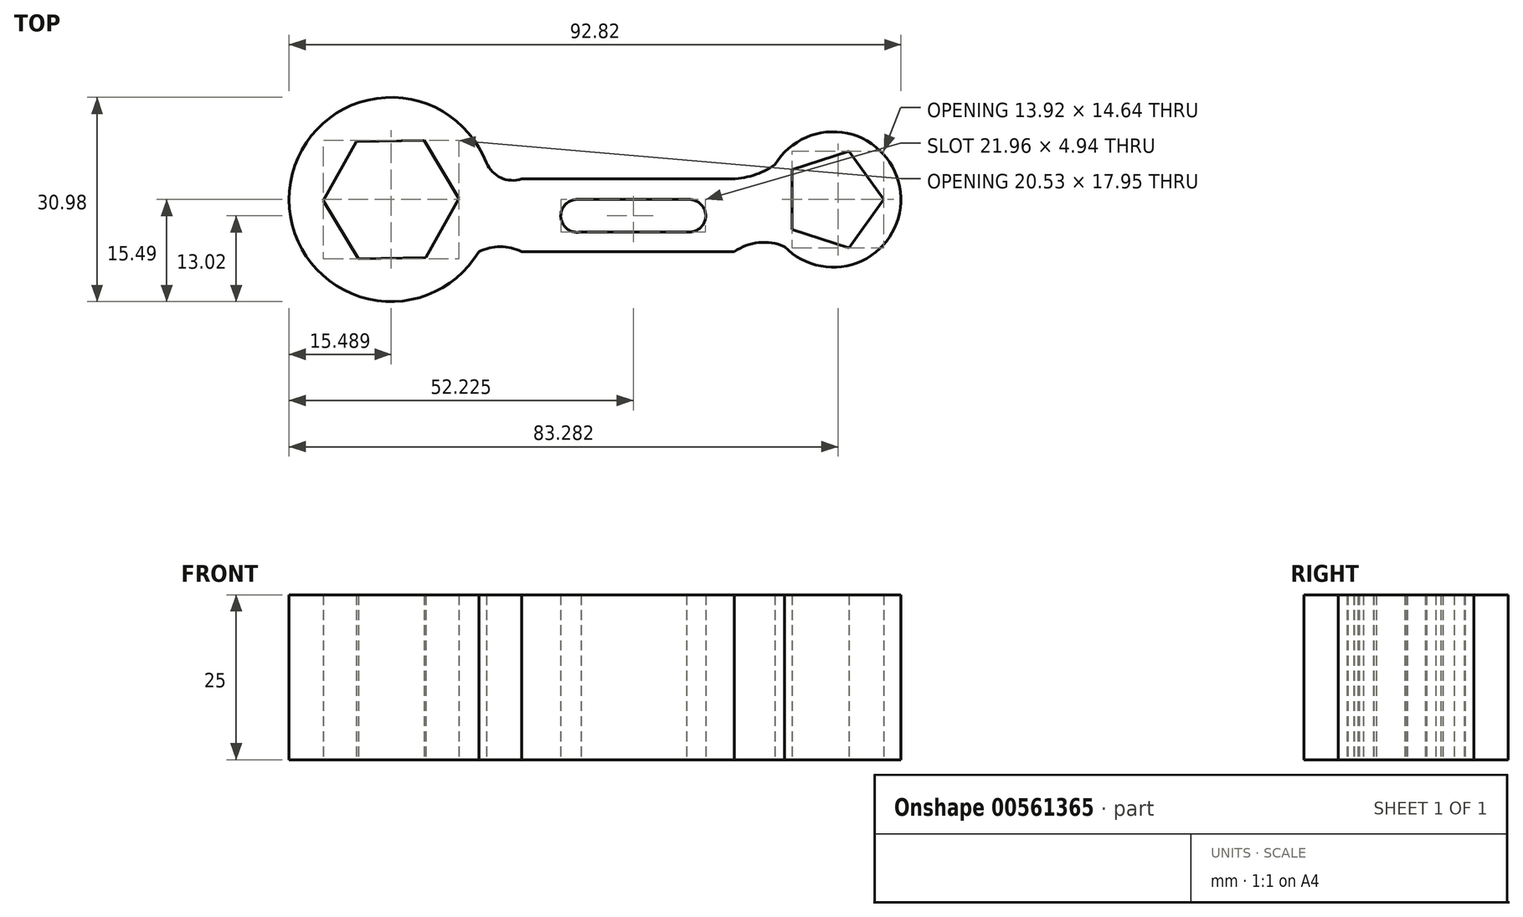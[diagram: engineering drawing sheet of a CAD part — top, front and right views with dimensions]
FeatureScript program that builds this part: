
annotation { "Feature Type Name" : "Feature", "Feature Type Description" : "" }
export const myFeature = defineFeature(function(context is Context, id is Id, definition is map)
    precondition{}
    {
        {
            var Q0;
            Q0=qCreatedBy(makeId("Top.planeOp"),FACE);
            var sketch = newSketch(context, id + "F0", { "sketchPlane" : qUnion([Q0])});
            skCircle(sketch, "E0", {"center": v(42.3, 0) * mm, "radius": 10.27 * mm});
            skCircle(sketch, "E1", {"center": v(-24.75, 0) * mm, "radius": 15.49 * mm});
            skLineSegment(sketch, "E2.0", {"start": v(-14.49, 0.17) * mm, "end": v(-19.47, -8.8) * mm});
            skLineSegment(sketch, "E2.1", {"start": v(-19.47, -8.8) * mm, "end": v(-29.74, -8.97) * mm});
            skLineSegment(sketch, "E2.2", {"start": v(-29.74, -8.97) * mm, "end": v(-35.01, -0.17) * mm});
            skLineSegment(sketch, "E2.3", {"start": v(-35.01, -0.17) * mm, "end": v(-30.03, 8.8) * mm});
            skLineSegment(sketch, "E2.4", {"start": v(-30.03, 8.8) * mm, "end": v(-19.77, 8.97) * mm});
            skLineSegment(sketch, "E2.5", {"start": v(-19.77, 8.97) * mm, "end": v(-14.49, 0.17) * mm});
            skPoint(sketch, "E2.0.midPoint", {"position": v(-16.98, -4.32) * mm});
            skArc(sketch, "E3.cCircle", {"start": v(46.8, 6.24) * mm, "mid": v(46.68, 6.33) * mm, "end": v(46.55, 6.42) * mm, "construction": true});
            skLineSegment(sketch, "E3.0", {"start": v(50, 0) * mm, "end": v(44.69, -7.32) * mm});
            skLineSegment(sketch, "E3.1", {"start": v(44.69, -7.32) * mm, "end": v(36.08, -4.52) * mm});
            skLineSegment(sketch, "E3.2", {"start": v(36.08, -4.52) * mm, "end": v(36.08, 4.52) * mm});
            skLineSegment(sketch, "E3.3", {"start": v(36.08, 4.52) * mm, "end": v(44.69, 7.32) * mm});
            skLineSegment(sketch, "E3.4", {"start": v(44.69, 7.32) * mm, "end": v(50, 0) * mm});
            skArc(sketch, "E4.cCircle", {"start": v(45.87, 5.26) * mm, "mid": v(46.41, 5.68) * mm, "end": v(46.8, 6.24) * mm, "construction": true});
            skLineSegment(sketch, "E4.0", {"start": v(42.3, 7.32) * mm, "end": v(42.52, 7.7) * mm});
            skLineSegment(sketch, "E4.3", {"start": v(46.55, 6.42) * mm, "end": v(45.87, 5.26) * mm});
            skPoint(sketch, "E5.orphan", {"position": v(47.06, 7.32) * mm});
            skPoint(sketch, "E6.orphan", {"position": v(43.5, 5.26) * mm});
            skArc(sketch, "E7.trimOffspring", {"start": v(42.52, 7.7) * mm, "mid": v(42.43, 7.7) * mm, "end": v(42.34, 7.7) * mm, "construction": true});
            skArc(sketch, "E8", {"start": v(-10.38, 5.78) * mm, "mid": v(-8.2, 3.34) * mm, "end": v(-4.94, 3.1) * mm});
            skArc(sketch, "E9", {"start": v(-4.94, -7.91) * mm, "mid": v(-8.18, -7.17) * mm, "end": v(-11.43, -7.9) * mm});
            skLineSegment(sketch, "E10", {"start": v(-4.94, 3.1) * mm, "end": v(26.53, 3.1) * mm});
            skLineSegment(sketch, "E11", {"start": v(-4.94, -7.91) * mm, "end": v(27.31, -7.91) * mm});
            skArc(sketch, "E12", {"start": v(26.53, 3.1) * mm, "mid": v(30.17, 3.66) * mm, "end": v(33.48, 5.26) * mm});
            skArc(sketch, "E13", {"start": v(37.76, -9.21) * mm, "mid": v(32.79, -6.55) * mm, "end": v(27.31, -7.91) * mm});
            skLineSegment(sketch, "E14", {"start": v(3.48, 0) * mm, "end": v(20.5, 0) * mm});
            skLineSegment(sketch, "E15", {"start": v(4.08, -4.9) * mm, "end": v(20.1, -4.9) * mm});
            skArc(sketch, "E16", {"start": v(3.48, 0) * mm, "mid": v(1, -2.8) * mm, "end": v(4.08, -4.9) * mm});
            skArc(sketch, "E17", {"start": v(20.1, -4.9) * mm, "mid": v(22.96, -2.67) * mm, "end": v(20.5, 0) * mm});
            skSolve(sketch);
        }
        {
            var Q0;
            Q0 = qSketchRegion(id + "F0", true);
            extrude(context, id + "F1", {"entities" : qUnion([Q0]), "depth" : 25 * mm, "offsetDistance" : 25 * mm});
        }
    });
